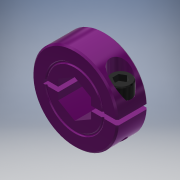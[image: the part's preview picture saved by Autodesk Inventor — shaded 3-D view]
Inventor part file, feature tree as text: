
AUTODESK INVENTOR PART (.ipt)
format: ipt  version: 2017.1 (Build 211199000, 199)  size: 310,272 bytes
history: native  units: in
note: dims shown in document units (in); Inventor stores cm internally (conversion verified against a paired STEP export)
features: extrude x2, sketch x2, other x1, imported_body x1
ambient origin geometry x8: Origin, YZ Plane, XZ Plane, XY Plane, X Axis, Y Axis, Z Axis, Center Point
bodies: Solid1 (feature_tree)
feature tree (6):
  other  "CL-8-A1"
  extrude  "Extrusion1"  Depth=0.4375in TaperAngle=0.0deg
  extrude  "Extrusion2"  [1 undecoded]
  imported_body  "Base1"
  sketch  "Sketch2"  dims[d0=0.5in d1=0.4375in d2=0.0in]
  sketch  "Sketch3"  dims[d3=1.0in d4=0.0in]
note: 1 required parameter value undecoded (feature->parameter linkage not recoverable at this tier; creation-order binding heuristic only, values carry confidence <= 0.55)
